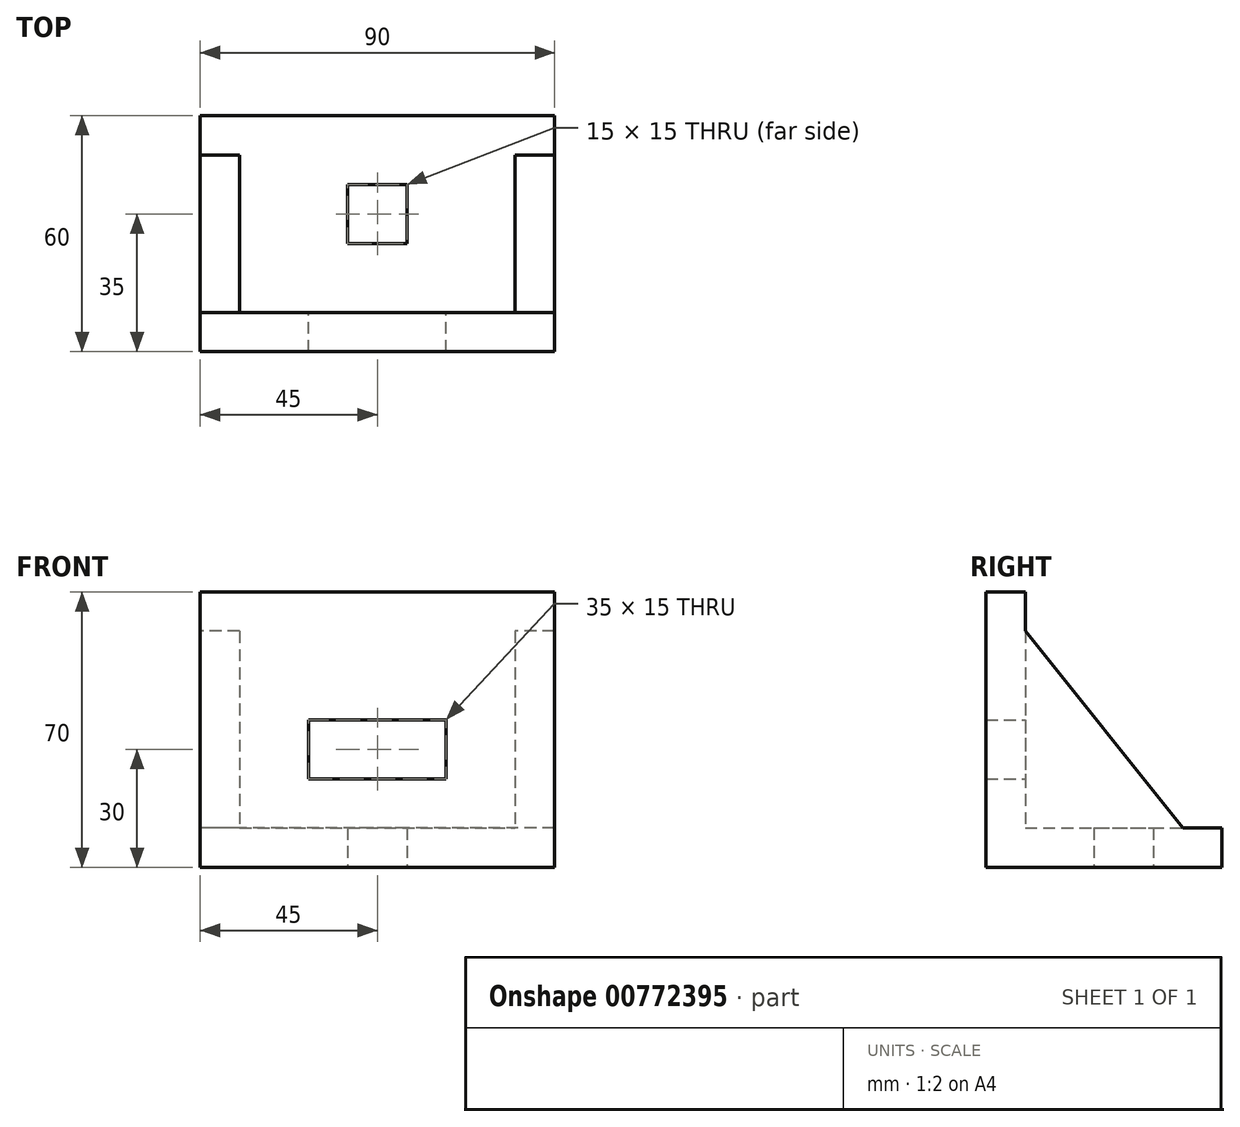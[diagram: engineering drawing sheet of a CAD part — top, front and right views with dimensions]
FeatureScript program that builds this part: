
annotation { "Feature Type Name" : "Feature", "Feature Type Description" : "" }
export const myFeature = defineFeature(function(context is Context, id is Id, definition is map)
    precondition{}
    {
        {
            var Q0;
            Q0=qCreatedBy(makeId("Right.planeOp"),FACE);
            var sketch = newSketch(context, id + "F0", { "sketchPlane" : qUnion([Q0])});
            skLineSegment(sketch, "E0", {"start": v(0, 0) * mm, "end": v(0, 70) * mm});
            skLineSegment(sketch, "E1", {"start": v(0, 70) * mm, "end": v(10, 70) * mm});
            skLineSegment(sketch, "E2", {"start": v(10, 70) * mm, "end": v(10, 60) * mm});
            skLineSegment(sketch, "E3", {"start": v(10, 60) * mm, "end": v(50, 10) * mm});
            skLineSegment(sketch, "E4", {"start": v(50, 10) * mm, "end": v(60, 10) * mm});
            skLineSegment(sketch, "E5", {"start": v(60, 10) * mm, "end": v(60, 0) * mm});
            skLineSegment(sketch, "E6", {"start": v(60, 0) * mm, "end": v(0, 0) * mm});
            skLineSegment(sketch, "E7", {"start": v(10, 60) * mm, "end": v(10, 10) * mm});
            skLineSegment(sketch, "E8", {"start": v(10, 10) * mm, "end": v(50, 10) * mm});
            skLineSegment(sketch, "E9", {"start": v(35, 10) * mm, "end": v(35, 0) * mm, "construction": true});
            skLineSegment(sketch, "E10", {"start": v(42.5, 10) * mm, "end": v(42.5, 0) * mm});
            skLineSegment(sketch, "E11.MirrorCS", {"start": v(27.5, 10) * mm, "end": v(27.5, 0) * mm});
            skLineSegment(sketch, "E12", {"start": v(0, 30) * mm, "end": v(10, 30) * mm, "construction": true});
            skLineSegment(sketch, "E13", {"start": v(0, 37.5) * mm, "end": v(10, 37.5) * mm});
            skLineSegment(sketch, "E14.MirrorCS", {"start": v(0, 22.5) * mm, "end": v(10, 22.5) * mm});
            skSolve(sketch);
        }
        {
            var Q0;
            Q0=qSketchRegion(id+"F0",true);
            extrude(context, id + "F1", {"entities" : qUnion([Q0]), "endBound" : BoundingType.SYMMETRIC, "depth" : 90 * mm, "offsetDistance" : 25 * mm});
        }
        {
            var Q0;
            {var subQ5=sQuery(id+"F0.wireOp",EDGE,"E3");Q0=makeQuery(id+"F0.imprint","IMPRINT",FACE,{"disambiguationData":[TD([[makeQuery(id+"F0.imprint","IMPRINT",EDGE,{"derivedFrom":subQ5}),-1.0]])]});}
            extrude(context, id + "F2", {"entities" : qUnion([Q0]), "operationType" : NewBodyOperationType.REMOVE, "endBound" : BoundingType.SYMMETRIC, "oppositeDirection" : true, "depth" : 70 * mm, "offsetDistance" : 25 * mm});
        }
        {
            var Q0;
            {var subQ0=sQuery(id+"F0.wireOp",EDGE,"E13");Q0=makeQuery(id+"F0.imprint","IMPRINT",FACE,{"disambiguationData":[TD([[makeQuery(id+"F0.imprint","IMPRINT",EDGE,{"derivedFrom":subQ0}),-1.0]])]});}
            extrude(context, id + "F3", {"entities" : qUnion([Q0]), "operationType" : NewBodyOperationType.REMOVE, "endBound" : BoundingType.SYMMETRIC, "depth" : 35 * mm, "offsetDistance" : 25 * mm});
        }
        {
            var Q0;
            {var subQ0=sQuery(id+"F0.wireOp",EDGE,"E10");Q0=makeQuery(id+"F0.imprint","IMPRINT",FACE,{"disambiguationData":[TD([[makeQuery(id+"F0.imprint","IMPRINT",EDGE,{"derivedFrom":subQ0}),-1.0]])]});}
            extrude(context, id + "F4", {"entities" : qUnion([Q0]), "operationType" : NewBodyOperationType.REMOVE, "endBound" : BoundingType.SYMMETRIC, "depth" : 15 * mm, "offsetDistance" : 25 * mm});
        }
    });
